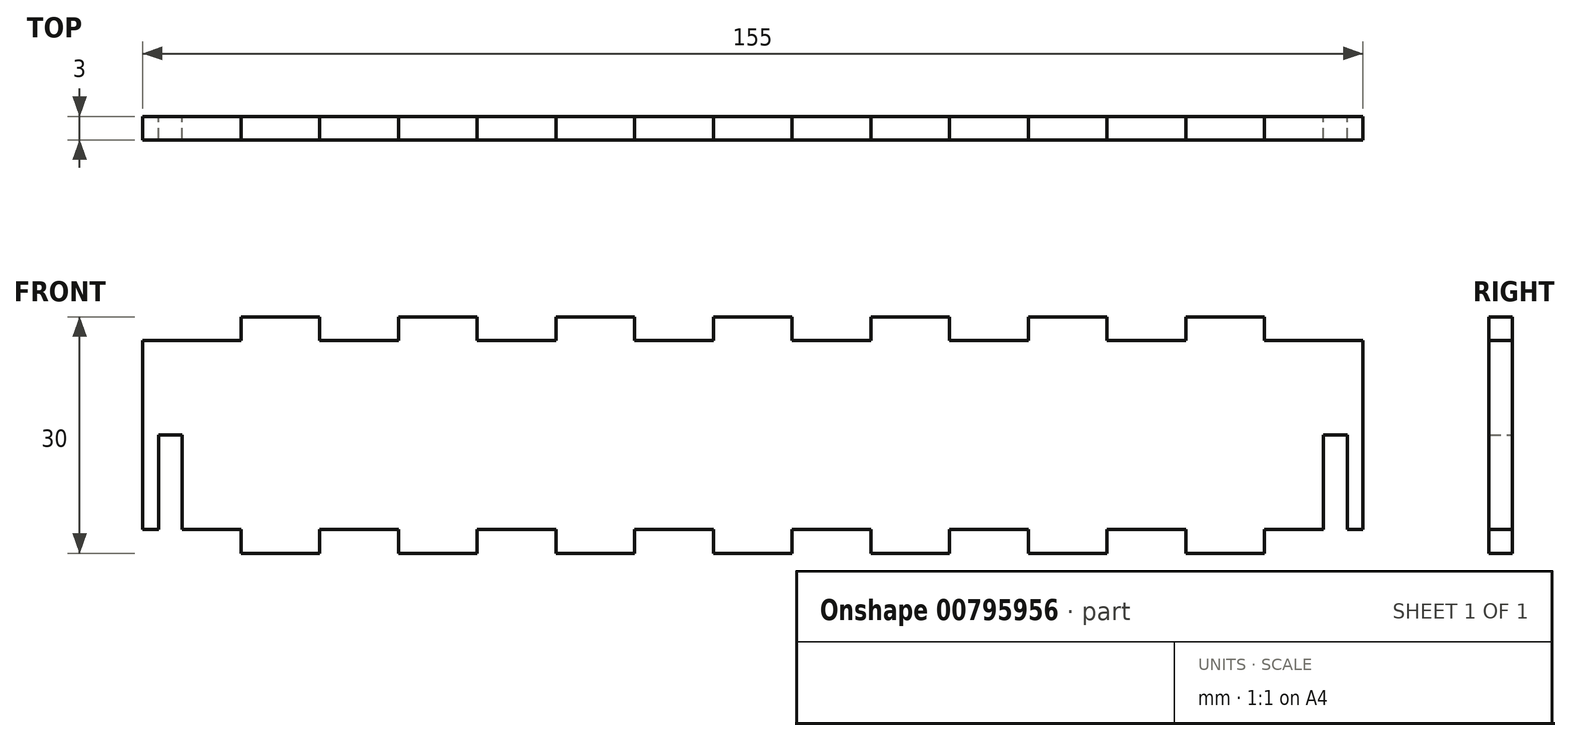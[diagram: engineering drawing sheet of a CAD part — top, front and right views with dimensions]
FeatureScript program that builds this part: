
annotation { "Feature Type Name" : "Feature", "Feature Type Description" : "" }
export const myFeature = defineFeature(function(context is Context, id is Id, definition is map)
    precondition{}
    {
        {
            var Q0;
            Q0=qCreatedBy(makeId("Front.planeOp"),FACE);
            var sketch = newSketch(context, id + "F0", { "sketchPlane" : qUnion([Q0])});
            skLineSegment(sketch, "E0.bottom", {"start": v(72.5, 15) * mm, "end": v(-72.5, 15) * mm});
            skLineSegment(sketch, "E0.top", {"start": v(72.5, -15) * mm, "end": v(-72.5, -15) * mm});
            skLineSegment(sketch, "E0.left", {"start": v(72.5, 15) * mm, "end": v(72.5, -15) * mm});
            skLineSegment(sketch, "E0.right", {"start": v(-72.5, 15) * mm, "end": v(-72.5, -15) * mm});
            skPoint(sketch, "E0.middle", {"position": v(0, 0) * mm});
            skSolve(sketch);
        }
        {
            var Q0;
            Q0=makeQuery(id+"F0.imprint","IMPRINT",FACE,{"disambiguationData":[TD([[makeQuery(id+"F0.imprint","IMPRINT",EDGE,{"derivedFrom":sQuery(id+"F0.wireOp",EDGE,"E0.bottom")}),1.0]])]});
            extrude(context, id + "F1", {"entities" : qUnion([Q0]), "depth" : 3 * mm, "offsetDistance" : 25 * mm});
        }
        {
            var Q0;
            Q0=makeQuery(id+"F1.opExtrude","CAP_FACE",FACE,{"disambiguationData":[OSD([sQuery(id+"F0.wireOp",EDGE,"E0.bottom"),sQuery(id+"F0.wireOp",EDGE,"E0.top"),sQuery(id+"F0.wireOp",EDGE,"E0.left"),sQuery(id+"F0.wireOp",EDGE,"E0.right")])],"isStart":false});
            var sketch = newSketch(context, id + "F2", { "sketchPlane" : qUnion([Q0])});
            skLineSegment(sketch, "E1", {"start": v(-75, -15) * mm, "end": v(-72.5, -15) * mm, "construction": true});
            skLineSegment(sketch, "E2.bottom", {"start": v(-75, -15) * mm, "end": v(-65, -15) * mm});
            skLineSegment(sketch, "E2.top", {"start": v(-75, -12) * mm, "end": v(-65, -12) * mm});
            skLineSegment(sketch, "E2.left", {"start": v(-75, -15) * mm, "end": v(-75, -12) * mm});
            skLineSegment(sketch, "E2.right", {"start": v(-65, -15) * mm, "end": v(-65, -12) * mm});
            skLineSegment(sketch, "E3.0.1.0", {"start": v(-75, 15) * mm, "end": v(-65, 15) * mm});
            skLineSegment(sketch, "E3.0.1.1", {"start": v(-75, 12) * mm, "end": v(-65, 12) * mm});
            skLineSegment(sketch, "E3.0.1.2", {"start": v(-65, 12) * mm, "end": v(-65, 15) * mm});
            skLineSegment(sketch, "E3.0.1.3", {"start": v(-75, 12) * mm, "end": v(-75, 15) * mm});
            skLineSegment(sketch, "E3.1.0.0", {"start": v(-55, -12) * mm, "end": v(-45, -12) * mm});
            skLineSegment(sketch, "E3.1.0.1", {"start": v(-55, -15) * mm, "end": v(-45, -15) * mm});
            skLineSegment(sketch, "E3.1.0.2", {"start": v(-45, -15) * mm, "end": v(-45, -12) * mm});
            skLineSegment(sketch, "E3.1.0.3", {"start": v(-55, -15) * mm, "end": v(-55, -12) * mm});
            skLineSegment(sketch, "E3.1.1.0", {"start": v(-55, 15) * mm, "end": v(-45, 15) * mm});
            skLineSegment(sketch, "E3.1.1.1", {"start": v(-55, 12) * mm, "end": v(-45, 12) * mm});
            skLineSegment(sketch, "E3.1.1.2", {"start": v(-45, 12) * mm, "end": v(-45, 15) * mm});
            skLineSegment(sketch, "E3.1.1.3", {"start": v(-55, 12) * mm, "end": v(-55, 15) * mm});
            skLineSegment(sketch, "E3.2.0.0", {"start": v(-35, -12) * mm, "end": v(-25, -12) * mm});
            skLineSegment(sketch, "E3.2.0.1", {"start": v(-35, -15) * mm, "end": v(-25, -15) * mm});
            skLineSegment(sketch, "E3.2.0.2", {"start": v(-25, -15) * mm, "end": v(-25, -12) * mm});
            skLineSegment(sketch, "E3.2.0.3", {"start": v(-35, -15) * mm, "end": v(-35, -12) * mm});
            skLineSegment(sketch, "E3.2.1.0", {"start": v(-35, 15) * mm, "end": v(-25, 15) * mm});
            skLineSegment(sketch, "E3.2.1.1", {"start": v(-35, 12) * mm, "end": v(-25, 12) * mm});
            skLineSegment(sketch, "E3.2.1.2", {"start": v(-25, 12) * mm, "end": v(-25, 15) * mm});
            skLineSegment(sketch, "E3.2.1.3", {"start": v(-35, 12) * mm, "end": v(-35, 15) * mm});
            skLineSegment(sketch, "E3.3.0.0", {"start": v(-15, -12) * mm, "end": v(-5, -12) * mm});
            skLineSegment(sketch, "E3.3.0.1", {"start": v(-15, -15) * mm, "end": v(-5, -15) * mm});
            skLineSegment(sketch, "E3.3.0.2", {"start": v(-5, -15) * mm, "end": v(-5, -12) * mm});
            skLineSegment(sketch, "E3.3.0.3", {"start": v(-15, -15) * mm, "end": v(-15, -12) * mm});
            skLineSegment(sketch, "E3.3.1.0", {"start": v(-15, 15) * mm, "end": v(-5, 15) * mm});
            skLineSegment(sketch, "E3.3.1.1", {"start": v(-15, 12) * mm, "end": v(-5, 12) * mm});
            skLineSegment(sketch, "E3.3.1.2", {"start": v(-5, 12) * mm, "end": v(-5, 15) * mm});
            skLineSegment(sketch, "E3.3.1.3", {"start": v(-15, 12) * mm, "end": v(-15, 15) * mm});
            skLineSegment(sketch, "E3.4.0.0", {"start": v(5, -12) * mm, "end": v(15, -12) * mm});
            skLineSegment(sketch, "E3.4.0.1", {"start": v(5, -15) * mm, "end": v(15, -15) * mm});
            skLineSegment(sketch, "E3.4.0.2", {"start": v(15, -15) * mm, "end": v(15, -12) * mm});
            skLineSegment(sketch, "E3.4.0.3", {"start": v(5, -15) * mm, "end": v(5, -12) * mm});
            skLineSegment(sketch, "E3.4.1.0", {"start": v(5, 15) * mm, "end": v(15, 15) * mm});
            skLineSegment(sketch, "E3.4.1.1", {"start": v(5, 12) * mm, "end": v(15, 12) * mm});
            skLineSegment(sketch, "E3.4.1.2", {"start": v(15, 12) * mm, "end": v(15, 15) * mm});
            skLineSegment(sketch, "E3.4.1.3", {"start": v(5, 12) * mm, "end": v(5, 15) * mm});
            skLineSegment(sketch, "E3.5.0.0", {"start": v(25, -12) * mm, "end": v(35, -12) * mm});
            skLineSegment(sketch, "E3.5.0.1", {"start": v(25, -15) * mm, "end": v(35, -15) * mm});
            skLineSegment(sketch, "E3.5.0.2", {"start": v(35, -15) * mm, "end": v(35, -12) * mm});
            skLineSegment(sketch, "E3.5.0.3", {"start": v(25, -15) * mm, "end": v(25, -12) * mm});
            skLineSegment(sketch, "E3.5.1.0", {"start": v(25, 15) * mm, "end": v(35, 15) * mm});
            skLineSegment(sketch, "E3.5.1.1", {"start": v(25, 12) * mm, "end": v(35, 12) * mm});
            skLineSegment(sketch, "E3.5.1.2", {"start": v(35, 12) * mm, "end": v(35, 15) * mm});
            skLineSegment(sketch, "E3.5.1.3", {"start": v(25, 12) * mm, "end": v(25, 15) * mm});
            skLineSegment(sketch, "E3.6.0.0", {"start": v(45, -12) * mm, "end": v(55, -12) * mm});
            skLineSegment(sketch, "E3.6.0.1", {"start": v(45, -15) * mm, "end": v(55, -15) * mm});
            skLineSegment(sketch, "E3.6.0.2", {"start": v(55, -15) * mm, "end": v(55, -12) * mm});
            skLineSegment(sketch, "E3.6.0.3", {"start": v(45, -15) * mm, "end": v(45, -12) * mm});
            skLineSegment(sketch, "E3.6.1.0", {"start": v(45, 15) * mm, "end": v(55, 15) * mm});
            skLineSegment(sketch, "E3.6.1.1", {"start": v(45, 12) * mm, "end": v(55, 12) * mm});
            skLineSegment(sketch, "E3.6.1.2", {"start": v(55, 12) * mm, "end": v(55, 15) * mm});
            skLineSegment(sketch, "E3.6.1.3", {"start": v(45, 12) * mm, "end": v(45, 15) * mm});
            skLineSegment(sketch, "E3.direction1", {"start": v(-75, -12) * mm, "end": v(-55, -12) * mm, "construction": true});
            skLineSegment(sketch, "E3.direction2", {"start": v(-75, -12) * mm, "end": v(-75, 15) * mm, "construction": true});
            skLineSegment(sketch, "E4.0.7.0", {"start": v(65, -12) * mm, "end": v(75, -12) * mm});
            skLineSegment(sketch, "E4.3.7.0", {"start": v(65, -15) * mm, "end": v(75, -15) * mm});
            skLineSegment(sketch, "E4.6.7.0", {"start": v(75, -15) * mm, "end": v(75, -12) * mm});
            skLineSegment(sketch, "E4.9.7.0", {"start": v(65, -15) * mm, "end": v(65, -12) * mm});
            skLineSegment(sketch, "E4.0.7.1", {"start": v(65, 15) * mm, "end": v(75, 15) * mm});
            skLineSegment(sketch, "E4.3.7.1", {"start": v(65, 12) * mm, "end": v(75, 12) * mm});
            skLineSegment(sketch, "E4.6.7.1", {"start": v(75, 12) * mm, "end": v(75, 15) * mm});
            skLineSegment(sketch, "E4.9.7.1", {"start": v(65, 12) * mm, "end": v(65, 15) * mm});
            skSolve(sketch);
        }
        {
            var Q0;
            Q0=qSketchRegion(id+"F2",true);
            extrude(context, id + "F3", {"entities" : qUnion([Q0]), "operationType" : NewBodyOperationType.REMOVE, "oppositeDirection" : true, "depth" : 25 * mm, "offsetDistance" : 25 * mm});
        }
        {
            var Q0;
            Q0=makeQuery(id+"F1.opExtrude","SWEPT_FACE",FACE,{"disambiguationData":[OSD([sQuery(id+"F0.wireOp",EDGE,"E0.left")])]});
            var Q1;
            Q1=makeQuery(id+"F1.opExtrude","SWEPT_FACE",FACE,{"disambiguationData":[OSD([sQuery(id+"F0.wireOp",EDGE,"E0.right")])]});
            extrude(context, id + "F4", {"entities" : qUnion([Q0, Q1]), "operationType" : NewBodyOperationType.ADD, "depth" : 5 * mm, "offsetDistance" : 25 * mm});
        }
        {
            var Q0;
            Q0=makeQuery(id+"F1.opExtrude","SWEPT_FACE",FACE,{"disambiguationData":[OSD([sQuery(id+"F0.wireOp",EDGE,"E0.right")])]});
            extrude(context, id + "F5", {"entities" : qUnion([Q0]), "operationType" : NewBodyOperationType.ADD, "depth" : 5 * mm, "offsetDistance" : 25 * mm});
        }
        {
            var Q0;
            {var subQ0=sQuery(id+"F0.wireOp",EDGE,"E0.right");var subQ1=sQuery(id+"F0.wireOp",EDGE,"E0.left");Q0=makeQuery(id+"F5.boolean.opBoolean","MERGE",FACE,{"derivedFrom":[makeQuery(id+"F4.boolean.opBoolean","MERGE",FACE,{"derivedFrom":[makeQuery(id+"F1.opExtrude","CAP_FACE",FACE,{"disambiguationData":[OSD([sQuery(id+"F0.wireOp",EDGE,"E0.bottom"),sQuery(id+"F0.wireOp",EDGE,"E0.top"),subQ1,subQ0])],"isStart":true}),makeQuery(id+"F4.opExtrude","SWEPT_FACE",FACE,{"disambiguationData":[OSD([subQ1]),TDD([makeQuery(id+"F1.opExtrude","CAP_EDGE",EDGE,{"disambiguationData":[OSD([subQ1])],"isStart":true})])]})]}),makeQuery(id+"F5.opExtrude","SWEPT_FACE",FACE,{"disambiguationData":[OSD([subQ0]),TDD([makeQuery(id+"F1.opExtrude","CAP_EDGE",EDGE,{"disambiguationData":[OSD([subQ0])],"isStart":true})])]})]});}
            var sketch = newSketch(context, id + "F6", { "sketchPlane" : qUnion([Q0])});
            skLineSegment(sketch, "E5.bottom", {"start": v(75.5, -12) * mm, "end": v(72.5, -12) * mm});
            skLineSegment(sketch, "E5.top", {"start": v(75.5, 0) * mm, "end": v(72.5, 0) * mm});
            skLineSegment(sketch, "E5.left", {"start": v(75.5, -12) * mm, "end": v(75.5, 0) * mm});
            skLineSegment(sketch, "E5.right", {"start": v(72.5, -12) * mm, "end": v(72.5, 0) * mm});
            skLineSegment(sketch, "E6", {"start": v(0, 15) * mm, "end": v(0, -24.82) * mm, "construction": true});
            skLineSegment(sketch, "E7.MirrorCS", {"start": v(-75.5, -12) * mm, "end": v(-75.5, 0) * mm});
            skLineSegment(sketch, "E8.MirrorCS", {"start": v(-75.5, 0) * mm, "end": v(-72.5, 0) * mm});
            skLineSegment(sketch, "E9.MirrorCS", {"start": v(-75.5, -12) * mm, "end": v(-72.5, -12) * mm});
            skLineSegment(sketch, "E10.MirrorCS", {"start": v(-72.5, -12) * mm, "end": v(-72.5, 0) * mm});
            skSolve(sketch);
        }
        {
            var Q0;
            Q0=makeQuery(id+"F6.imprint","IMPRINT",FACE,{"disambiguationData":[TD([[makeQuery(id+"F6.imprint","IMPRINT",EDGE,{"derivedFrom":sQuery(id+"F6.wireOp",EDGE,"E7.MirrorCS")}),-1.0]])]});
            var Q1;
            Q1=makeQuery(id+"F6.imprint","IMPRINT",FACE,{"disambiguationData":[TD([[makeQuery(id+"F6.imprint","IMPRINT",EDGE,{"derivedFrom":sQuery(id+"F6.wireOp",EDGE,"E5.bottom")}),-1.0]])]});
            extrude(context, id + "F7", {"entities" : qUnion([Q0, Q1]), "operationType" : NewBodyOperationType.REMOVE, "oppositeDirection" : true, "depth" : 25 * mm, "offsetDistance" : 25 * mm});
        }
    });
